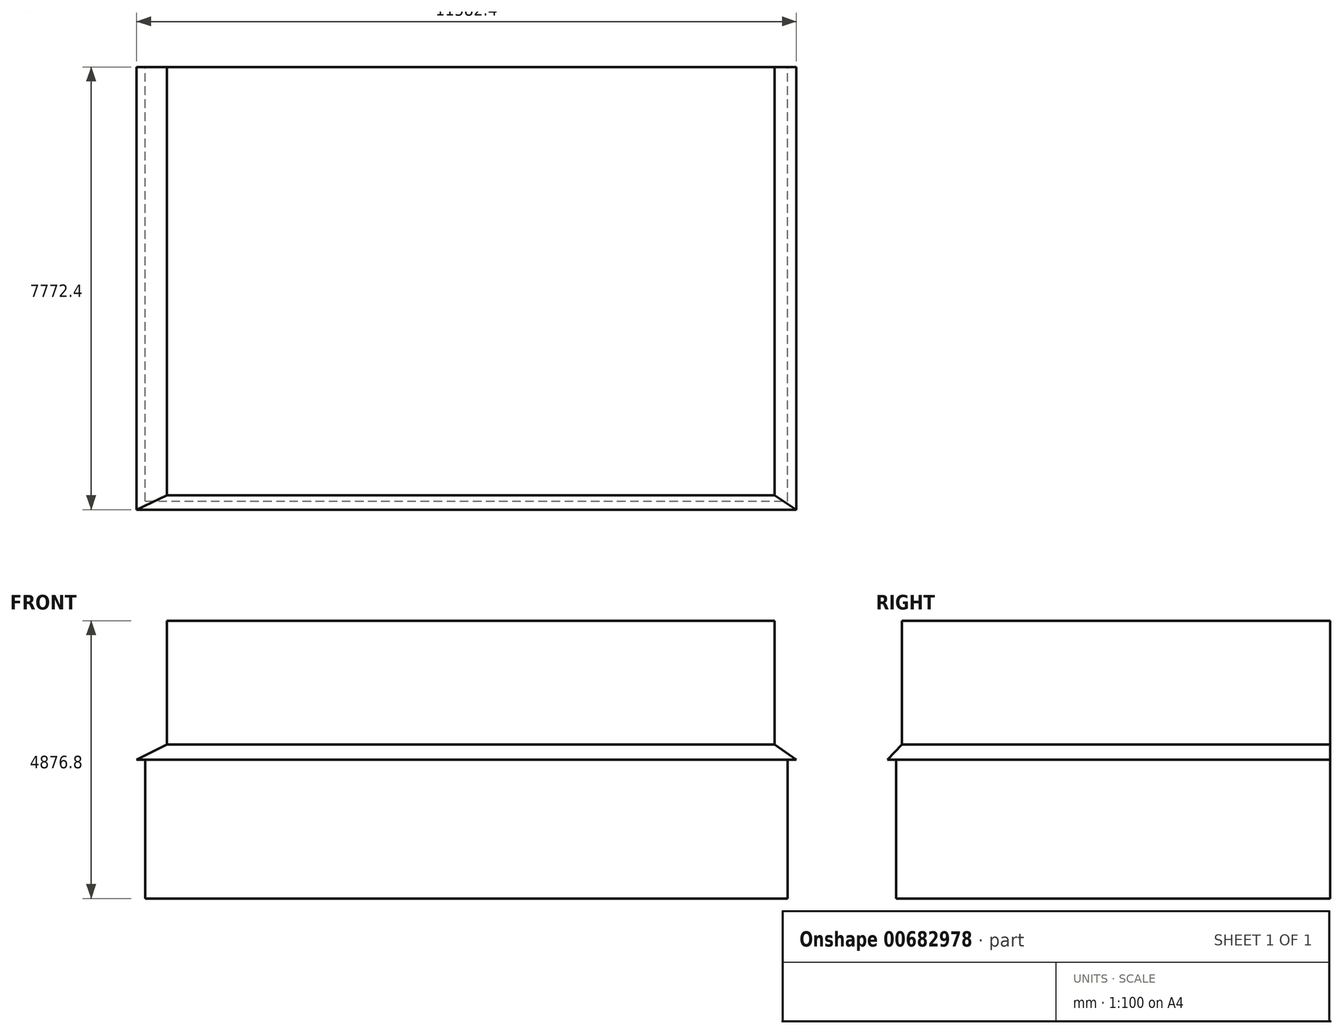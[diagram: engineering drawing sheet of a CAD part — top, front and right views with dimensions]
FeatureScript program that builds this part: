
annotation { "Feature Type Name" : "Feature", "Feature Type Description" : "" }
export const myFeature = defineFeature(function(context is Context, id is Id, definition is map)
    precondition{}
    {
        {
            var Q0;
            Q0=qCreatedBy(makeId("Top.planeOp"),FACE);
            var sketch = newSketch(context, id + "F0", { "sketchPlane" : qUnion([Q0])});
            skLineSegment(sketch, "E0.bottom", {"start": v(0, 0) * mm, "end": v(11277.6, 0) * mm});
            skLineSegment(sketch, "E0.top", {"start": v(0, 7620) * mm, "end": v(11277.6, 7620) * mm});
            skLineSegment(sketch, "E0.left", {"start": v(0, 0) * mm, "end": v(0, 7620) * mm});
            skLineSegment(sketch, "E0.right", {"start": v(11277.6, 0) * mm, "end": v(11277.6, 7620) * mm});
            skSolve(sketch);
        }
        {
            var Q0;
            Q0=makeQuery(id+"F0.imprint","IMPRINT",FACE,{"disambiguationData":[TD([[makeQuery(id+"F0.imprint","IMPRINT",EDGE,{"derivedFrom":sQuery(id+"F0.wireOp",EDGE,"E0.bottom")}),1.0]])]});
            extrude(context, id + "F1", {"entities" : qUnion([Q0]), "depth" : 2438.4 * mm, "offsetDistance" : 25.4 * mm});
        }
        {
            var Q0;
            Q0=makeQuery(id+"F1.opExtrude","CAP_FACE",FACE,{"disambiguationData":[OSD([sQuery(id+"F0.wireOp",EDGE,"E0.bottom"),sQuery(id+"F0.wireOp",EDGE,"E0.top"),sQuery(id+"F0.wireOp",EDGE,"E0.left"),sQuery(id+"F0.wireOp",EDGE,"E0.right")])],"isStart":false});
            var sketch = newSketch(context, id + "F2", { "sketchPlane" : qUnion([Q0])});
            skLineSegment(sketch, "E1.bottom", {"start": v(381, 101.6) * mm, "end": v(11049, 101.6) * mm});
            skLineSegment(sketch, "E1.top", {"start": v(381, 7620) * mm, "end": v(11049, 7620) * mm});
            skLineSegment(sketch, "E1.left", {"start": v(381, 101.6) * mm, "end": v(381, 7620) * mm});
            skLineSegment(sketch, "E1.right", {"start": v(11049, 101.6) * mm, "end": v(11049, 7620) * mm});
            skSolve(sketch);
        }
        {
            var Q0;
            Q0 = qSketchRegion(id + "F2", true);
            extrude(context, id + "F3", {"entities" : qUnion([Q0]), "depth" : 2438.4 * mm, "offsetDistance" : 25.4 * mm});
        }
        {
            var Q0;
            Q0=qCreatedBy(makeId("Front.planeOp"),FACE);
            var sketch = newSketch(context, id + "F4", { "sketchPlane" : qUnion([Q0])});
            skLineSegment(sketch, "E2", {"start": v(-152.4, 2438.4) * mm, "end": v(11430, 2438.4) * mm});
            skLineSegment(sketch, "E3", {"start": v(11430, 2438.4) * mm, "end": v(11049, 2705.1) * mm});
            skLineSegment(sketch, "E4", {"start": v(11049, 2705.1) * mm, "end": v(381, 2705.1) * mm});
            skLineSegment(sketch, "E5", {"start": v(381, 2705.1) * mm, "end": v(-152.4, 2438.4) * mm});
            skSolve(sketch);
        }
        {
            var Q0;
            Q0 = qSketchRegion(id + "F4", true);
            var Q1;
            Q1=makeQuery(id+"F3.boolean.opBoolean","MERGE",FACE,{"derivedFrom":[makeQuery(id+"F1.opExtrude","SWEPT_FACE",FACE,{"disambiguationData":[OSD([sQuery(id+"F0.wireOp",EDGE,"E0.top")])]}),makeQuery(id+"F3.opExtrude","SWEPT_FACE",FACE,{"disambiguationData":[OSD([sQuery(id+"F2.wireOp",EDGE,"E1.top")])]})]});
            extrude(context, id + "F5", {"entities" : qUnion([Q0]), "operationType" : NewBodyOperationType.ADD, "endBound" : BoundingType.UP_TO_SURFACE, "oppositeDirection" : true, "depth" : 25.4 * mm, "endBoundEntityFace" : qUnion([Q1]), "offsetDistance" : 25.4 * mm, "hasSecondDirection" : true, "secondDirectionOppositeDirection" : false, "secondDirectionDepth" : 152.4 * mm});
        }
        {
            var Q0;
            Q0=qCreatedBy(makeId("Right.planeOp"),FACE);
            var sketch = newSketch(context, id + "F6", { "sketchPlane" : qUnion([Q0])});
            skLineSegment(sketch, "E6", {"start": v(-152.4, 2438.4) * mm, "end": v(101.6, 2705.1) * mm});
            skLineSegment(sketch, "E7", {"start": v(101.6, 2705.1) * mm, "end": v(-152.4, 2705.1) * mm});
            skLineSegment(sketch, "E8", {"start": v(-152.4, 2705.1) * mm, "end": v(-152.4, 2438.4) * mm});
            skSolve(sketch);
        }
        {
            var Q0;
            Q0=makeQuery(id+"F6.imprint","IMPRINT",FACE,{"disambiguationData":[TD([[makeQuery(id+"F6.imprint","IMPRINT",EDGE,{"derivedFrom":sQuery(id+"F6.wireOp",EDGE,"E6")}),1.0]])]});
            extrude(context, id + "F7", {"entities" : qUnion([Q0]), "operationType" : NewBodyOperationType.REMOVE, "endBound" : BoundingType.THROUGH_ALL, "depth" : 25.4 * mm, "offsetDistance" : 25.4 * mm, "hasSecondDirection" : true, "secondDirectionBound" : SecondDirectionBoundingType.THROUGH_ALL, "secondDirectionOppositeDirection" : true, "secondDirectionDepth" : 25.4 * mm});
        }
    });
